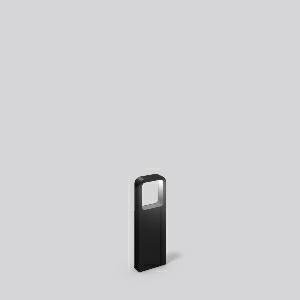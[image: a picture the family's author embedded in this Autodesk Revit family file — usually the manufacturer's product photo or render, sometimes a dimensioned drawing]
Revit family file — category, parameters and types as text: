
# Revit family: hb_202_611975_0031_0539
name_source: partatom
category: Lighting Fixtures
units: mm (PartAtom-declared; Revit-internal decimal feet)

## family parameters
Cut with Voids When Loaded = No
Host = Face
Light Source = No
Part Type = Normal
Room Calculation Point = No
Round Connector Dimension = Use Diameter
Shared = No

## types (1)
- HB 202 (1 x LED Modul 830, 290 lm, 3000)
    Apparent Load = 9 VA
    CIE Flux Codes = 44 77 95 99 100
    Color Rendering = 80
    Color Temperature = 3000
    Default Elevation = 1800 mm
    Description = Series: HB 202
Bollard for socket mounting. Housing: die-cast aluminium, powder-coated. Diffuser: plastic (polycarbonate), opal. Driver integrated. 
Colour: anthracite metallic (DB703)
Length: 40 mm
Width: 120 mm
Height: 350 mm
Lamp: LED
System power: 9 W
Rated luminous flux: 290 lm
Luminous efficiency: 32 lm/W
Control gear: Regulated power supply
Protection class: I
Type of protection: IP 54
    Height = 350 mm
    Lamp = 1 x LED Modul 830
    Lamp Light Flux = 290 lm
    Lamp count = 1
    Length = 40 mm  [stored 0.131234 ft]
    Lifetime = 50000 h
    Luminous efficacy = 32 lm/W
    Manufacturer = RZB
    ModVariant = No
    Model = 611975.0031
    Mounting Place = Floor
    Mounting Type = Freestanding
    Number of Poles = 1
    OnlyDefault = Yes
    Power Factor = 1
    Product Name = HB 202
    Product group = Bollards
    ProductGroupID = 1351
    Protection Class = Protection class I
    Protection Degree = IP 54
    RLX_Detail_Level = 1
    RLX_Emergency_Light_Flux = 0 lm
    RLX_Emergency_Type = 0
    RLX_Emergency_Type_DB = No
    RlxData = <blob elided: 22441 chars, md5=d16072b5>
    Socket = socket
    Standby Power = 0 W
    System Light Flux = 290 lm
    System Power = 9 W
    Type Comments = Product without accessories
    Type Image = 611975.0031.jpg
    URL = http://relux.com
    VarID = ---
    Voltage = 0 V
    Weight = 0.00 kg
    Width = 120 mm

note: [stored X ft] marks values corroborated as IEEE doubles in the binary element streams (Revit-internal decimal feet)

## geometry (parser evidence)
native form markers: Blend x4, Sweep x11
no freeform markers — native parametric forms only
